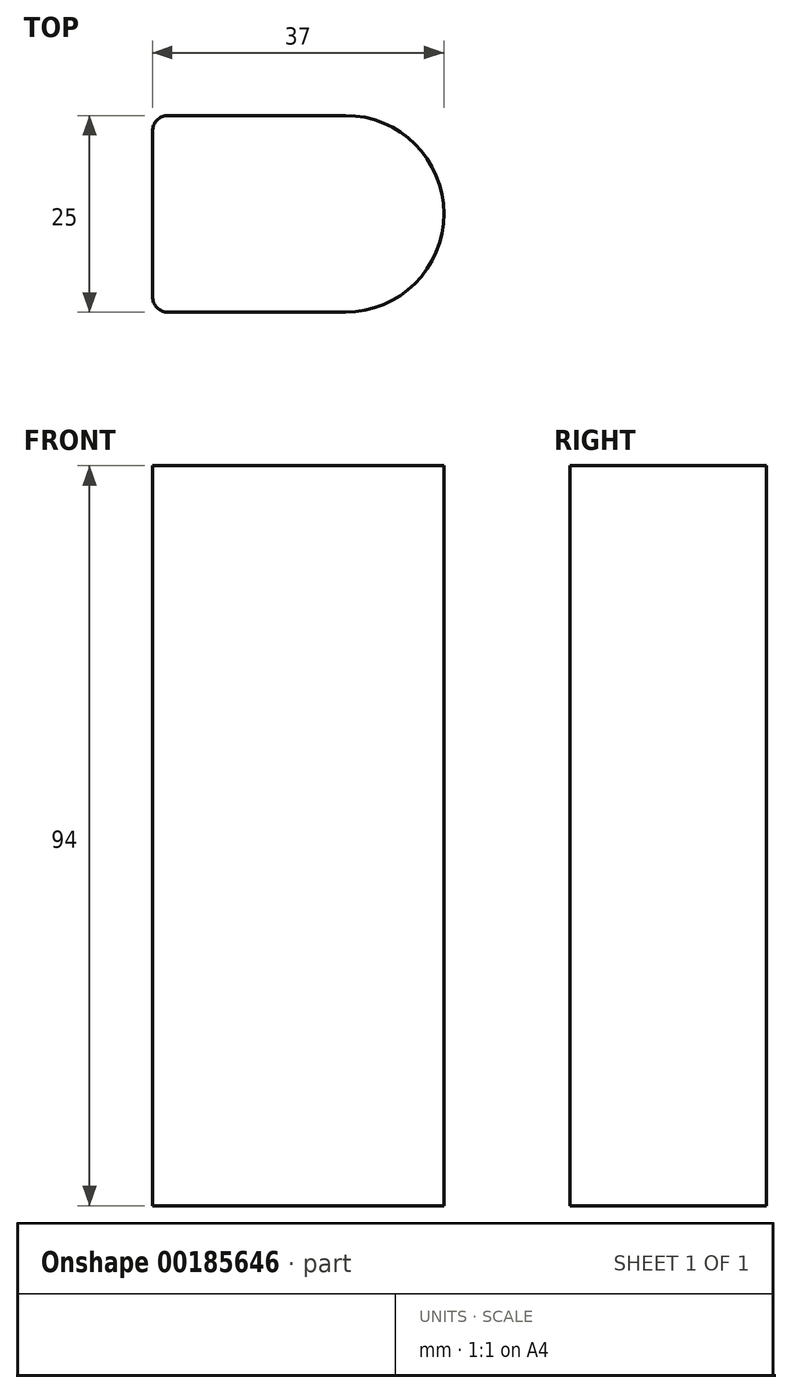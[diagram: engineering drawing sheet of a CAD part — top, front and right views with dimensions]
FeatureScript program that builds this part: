
annotation { "Feature Type Name" : "Feature", "Feature Type Description" : "" }
export const myFeature = defineFeature(function(context is Context, id is Id, definition is map)
    precondition{}
    {
        {
            var Q0;
            Q0=qCreatedBy(makeId("Top.planeOp"),FACE);
            var sketch = newSketch(context, id + "F0", { "sketchPlane" : qUnion([Q0])});
            skLineSegment(sketch, "E0.bottom", {"start": v(2, 12.5) * mm, "end": v(24.5, 12.5) * mm});
            skLineSegment(sketch, "E0.top", {"start": v(2, -12.5) * mm, "end": v(24.5, -12.5) * mm});
            skLineSegment(sketch, "E0.left", {"start": v(0, 10.5) * mm, "end": v(0, -10.5) * mm});
            skLineSegment(sketch, "E0.right", {"start": v(24.5, 12.5) * mm, "end": v(24.5, -12.5) * mm, "construction": true});
            skCircle(sketch, "E1", {"center": v(24.5, 0) * mm, "radius": 12.5 * mm});
            skLineSegment(sketch, "E2", {"start": v(0, 12.5) * mm, "end": v(0, 31.2) * mm, "construction": true});
            skLineSegment(sketch, "E3", {"start": v(0, 31.2) * mm, "end": v(37, 31.2) * mm, "construction": true});
            skLineSegment(sketch, "E4", {"start": v(37, 31.2) * mm, "end": v(37, 0) * mm, "construction": true});
            skPoint(sketch, "E5.visualSharp", {"position": v(0, 12.5) * mm});
            skArc(sketch, "E5.filletArc", {"start": v(2, 12.5) * mm, "mid": v(0.59, 11.91) * mm, "end": v(0, 10.5) * mm});
            skPoint(sketch, "E6.visualSharp", {"position": v(0, -12.5) * mm});
            skArc(sketch, "E6.filletArc", {"start": v(0, -10.5) * mm, "mid": v(0.59, -11.91) * mm, "end": v(2, -12.5) * mm});
            skSolve(sketch);
        }
        {
            var Q0;
            Q0 = qSketchRegion(id + "F0", true);
            extrude(context, id + "F1", {"entities" : qUnion([Q0]), "endBound" : BoundingType.SYMMETRIC, "depth" : 94 * mm});
        }
    });
